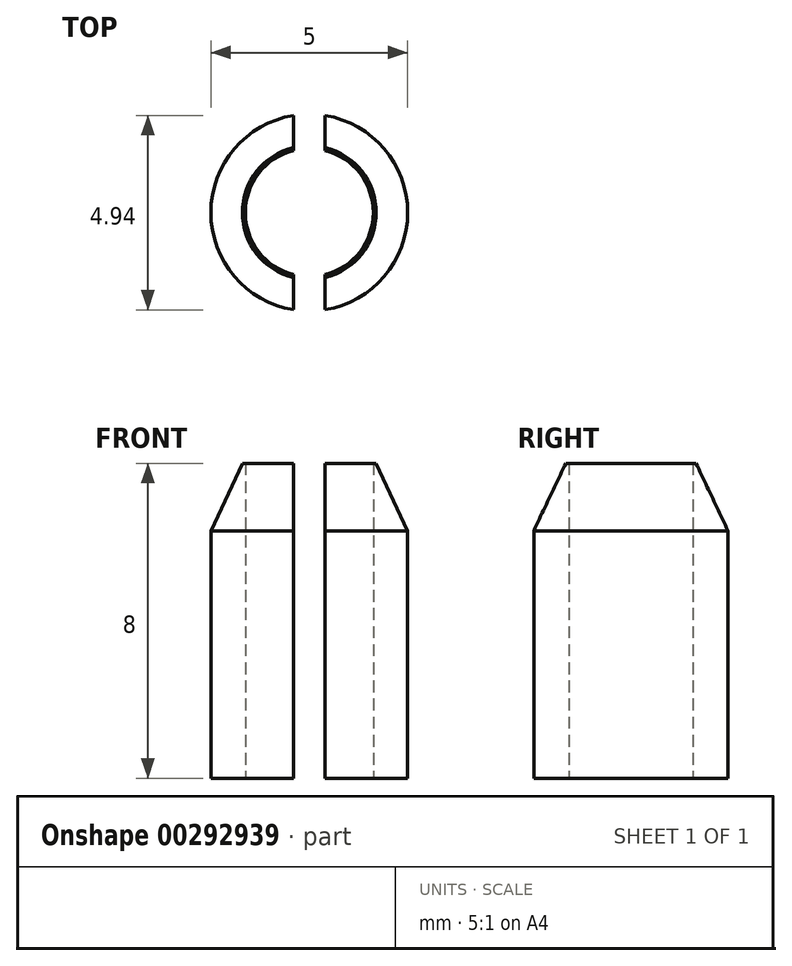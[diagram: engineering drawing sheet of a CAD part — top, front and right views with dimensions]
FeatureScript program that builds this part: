
annotation { "Feature Type Name" : "Feature", "Feature Type Description" : "" }
export const myFeature = defineFeature(function(context is Context, id is Id, definition is map)
    precondition{}
    {
        {
            var Q0;
            Q0=qCreatedBy(makeId("Top.planeOp"),FACE);
            var sketch = newSketch(context, id + "F0", { "sketchPlane" : qUnion([Q0])});
            skCircle(sketch, "E0", {"center": v(0, 0) * mm, "radius": 1.63 * mm});
            skCircle(sketch, "E1", {"center": v(0, 0) * mm, "radius": 2.5 * mm});
            skSolve(sketch);
        }
        {
            var Q0;
            Q0 = qSketchRegion(id + "F0", true);
            extrude(context, id + "F1", {"entities" : qUnion([Q0]), "depth" : 8 * mm});
        }
        {
            var Q0;
            Q0=qCreatedBy(makeId("Top.planeOp"),FACE);
            var sketch = newSketch(context, id + "F2", { "sketchPlane" : qUnion([Q0])});
            skLineSegment(sketch, "E2.bottom", {"start": v(-0.4, 2.95) * mm, "end": v(0.4, 2.95) * mm});
            skLineSegment(sketch, "E2.top", {"start": v(-0.4, -3.07) * mm, "end": v(0.4, -3.07) * mm});
            skLineSegment(sketch, "E2.left", {"start": v(-0.4, 2.95) * mm, "end": v(-0.4, -3.07) * mm});
            skLineSegment(sketch, "E2.right", {"start": v(0.4, 2.95) * mm, "end": v(0.4, -3.07) * mm});
            skSolve(sketch);
        }
        {
            var Q0;
            Q0 = qSketchRegion(id + "F2", true);
            extrude(context, id + "F3", {"entities" : qUnion([Q0]), "operationType" : NewBodyOperationType.REMOVE, "depth" : 25 * mm});
        }
        {
            var Q0;
            {var subQ0=sQuery(id+"F0.wireOp",EDGE,"E1");Q0=makeQuery(id+"F3.boolean.opBoolean","SPLIT",EDGE,{"disambiguationData":[TD([makeQuery(id+"F3.opExtrude","SWEPT_FACE",FACE,{"disambiguationData":[OSD([sQuery(id+"F2.wireOp",EDGE,"E2.right")])]})])],"derivedFrom":makeQuery(id+"F1.opExtrude","CAP_EDGE",EDGE,{"disambiguationData":[OSD([subQ0])],"isStart":false})});}
            var Q1;
            {var subQ0=sQuery(id+"F0.wireOp",EDGE,"E1");Q1=makeQuery(id+"F3.boolean.opBoolean","SPLIT",EDGE,{"disambiguationData":[TD([makeQuery(id+"F3.opExtrude","SWEPT_FACE",FACE,{"disambiguationData":[OSD([sQuery(id+"F2.wireOp",EDGE,"E2.left")])]})])],"derivedFrom":makeQuery(id+"F1.opExtrude","CAP_EDGE",EDGE,{"disambiguationData":[OSD([subQ0])],"isStart":false})});}
            chamfer(context, id + "F4", {"entities" : qUnion([Q0, Q1]), "chamferType" : ChamferType.OFFSET_ANGLE, "width" : .8 * mm, "oppositeDirection" : false, "angle" : 65 * degree, "tangentPropagation" : true});
        }
    });
